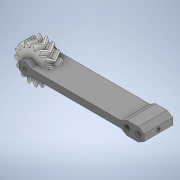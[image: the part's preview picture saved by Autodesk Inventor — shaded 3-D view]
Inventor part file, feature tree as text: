
AUTODESK INVENTOR PART (.ipt)
format: ipt  version: 2020 (Build 240168000, 168)  size: 966,144 bytes
history: native  units: in
note: dims shown in document units (in); Inventor stores cm internally (conversion verified against a paired STEP export)
features: sketch x4, other x3, extrude x3, plane x2, mirror x1, projected_geometry x1
ambient origin geometry x8: Origin, YZ Plane, XZ Plane, XY Plane, X Axis, Y Axis, Z Axis, Center Point
bodies: Solid1 (feature_tree), Solid2 (feature_tree)
feature tree (14):
  other  "Spur Gear1"
  plane  "Work Plane3"
  extrude  "Extrusion1"  Depth=3.4256in
  plane  "Work Plane1"
  extrude  "Extrusion2"  Depth=0.7874in
  sketch  "Sketch4"  dims[d4=0.0in d5=0.0906in]
  extrude  "Extrusion4"  Depth=0.0906in
  mirror  "Mirror3"
  sketch  "Sketch1"  dims[d0=0.1818in d1=3.4256in]
  sketch  "Sketch2"  dims[d2=0.0945in d3=0.7874in]
  sketch  "Sketch5"  dims[d6=0.7874in d7=0.0in d29=0.315in d31=0.315in d33=0.1476in d34=0.2362in d35=0.0in d38=0.315in d69=2.4807in d70=0.3937in d71=0.1969in]
  other  "Solid1::Spur Gear1"
  other  "TaggingFeature1"
  projected_geometry  "Projected Loop11"
